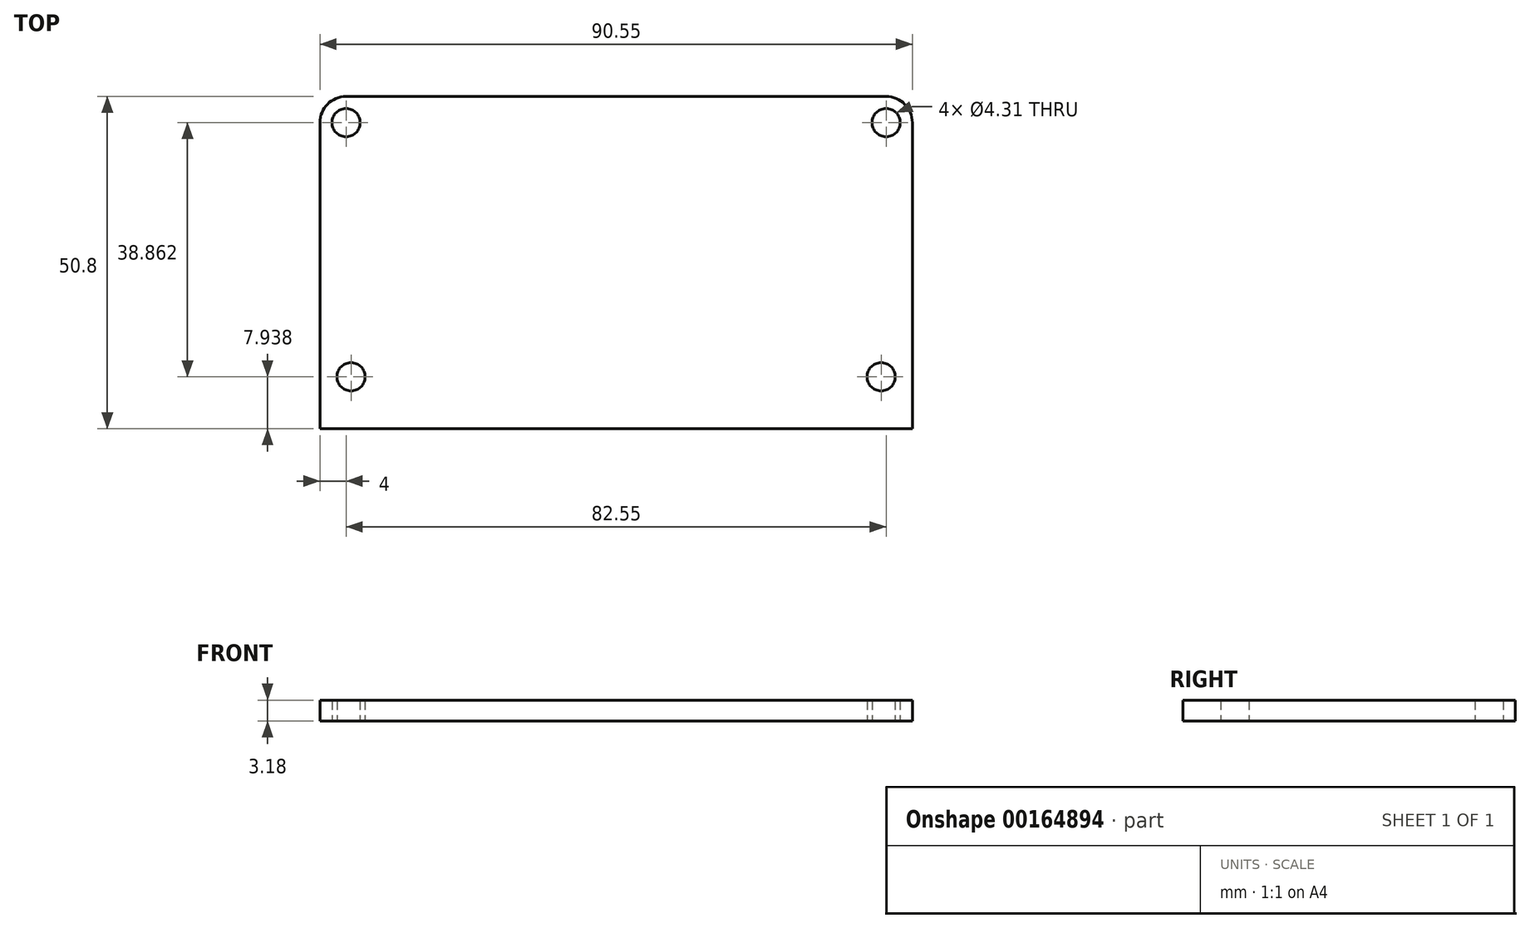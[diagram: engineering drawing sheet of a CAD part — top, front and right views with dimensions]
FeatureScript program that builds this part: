
annotation { "Feature Type Name" : "Feature", "Feature Type Description" : "" }
export const myFeature = defineFeature(function(context is Context, id is Id, definition is map)
    precondition{}
    {
        {
            var Q0;
            Q0=qCreatedBy(makeId("Top.planeOp"),FACE);
            var sketch = newSketch(context, id + "F0", { "sketchPlane" : qUnion([Q0])});
            skLineSegment(sketch, "E0.bottom", {"start": v(0, 0) * mm, "end": v(-90.55, 0) * mm});
            skLineSegment(sketch, "E0.top", {"start": v(0, -50.8) * mm, "end": v(-90.55, -50.8) * mm});
            skLineSegment(sketch, "E0.left", {"start": v(0, 0) * mm, "end": v(0, -50.8) * mm});
            skLineSegment(sketch, "E0.right", {"start": v(-90.55, 0) * mm, "end": v(-90.55, -50.8) * mm});
            skLineSegment(sketch, "E1", {"start": v(-45.27, 0) * mm, "end": v(-45.27, -4) * mm, "construction": true});
            skLineSegment(sketch, "E2", {"start": v(0, -4) * mm, "end": v(-4, -4) * mm, "construction": true});
            skLineSegment(sketch, "E3", {"start": v(-4, -4) * mm, "end": v(-86.55, -4) * mm, "construction": true});
            skCircle(sketch, "E4", {"center": v(-4, -4) * mm, "radius": 2.15 * mm});
            skCircle(sketch, "E5", {"center": v(-86.55, -4) * mm, "radius": 2.15 * mm});
            skLineSegment(sketch, "E6", {"start": v(-45.27, -50.8) * mm, "end": v(-45.27, -42.86) * mm, "construction": true});
            skLineSegment(sketch, "E7", {"start": v(-4.76, -42.86) * mm, "end": v(-85.79, -42.86) * mm, "construction": true});
            skLineSegment(sketch, "E8", {"start": v(-85.79, -42.86) * mm, "end": v(-90.55, -42.86) * mm, "construction": true});
            skCircle(sketch, "E9", {"center": v(-4.76, -42.86) * mm, "radius": 2.15 * mm});
            skCircle(sketch, "E10", {"center": v(-85.79, -42.86) * mm, "radius": 2.15 * mm});
            skSolve(sketch);
        }
        {
            var Q0;
            Q0 = qSketchRegion(id + "F0", true);
            extrude(context, id + "F1", {"entities" : qUnion([Q0]), "depth" : 3.17 * mm});
        }
        {
            var Q0;
            Q0=makeQuery(id+"F1.opExtrude","SWEPT_EDGE",EDGE,{"disambiguationData":[OSD([sQuery(id+"F0.wireOp",EDGE,"E0.bottom"),sQuery(id+"F0.wireOp",EDGE,"E0.left")])]});
            var Q1;
            Q1=makeQuery(id+"F1.opExtrude","SWEPT_EDGE",EDGE,{"disambiguationData":[OSD([sQuery(id+"F0.wireOp",EDGE,"E0.bottom"),sQuery(id+"F0.wireOp",EDGE,"E0.right")])]});
            fillet(context, id + "F2", {"entities" : qUnion([Q0, Q1]), "radius" : 4 * mm, "tangentPropagation" : true, "allowEdgeOverflow" : false});
        }
    });
